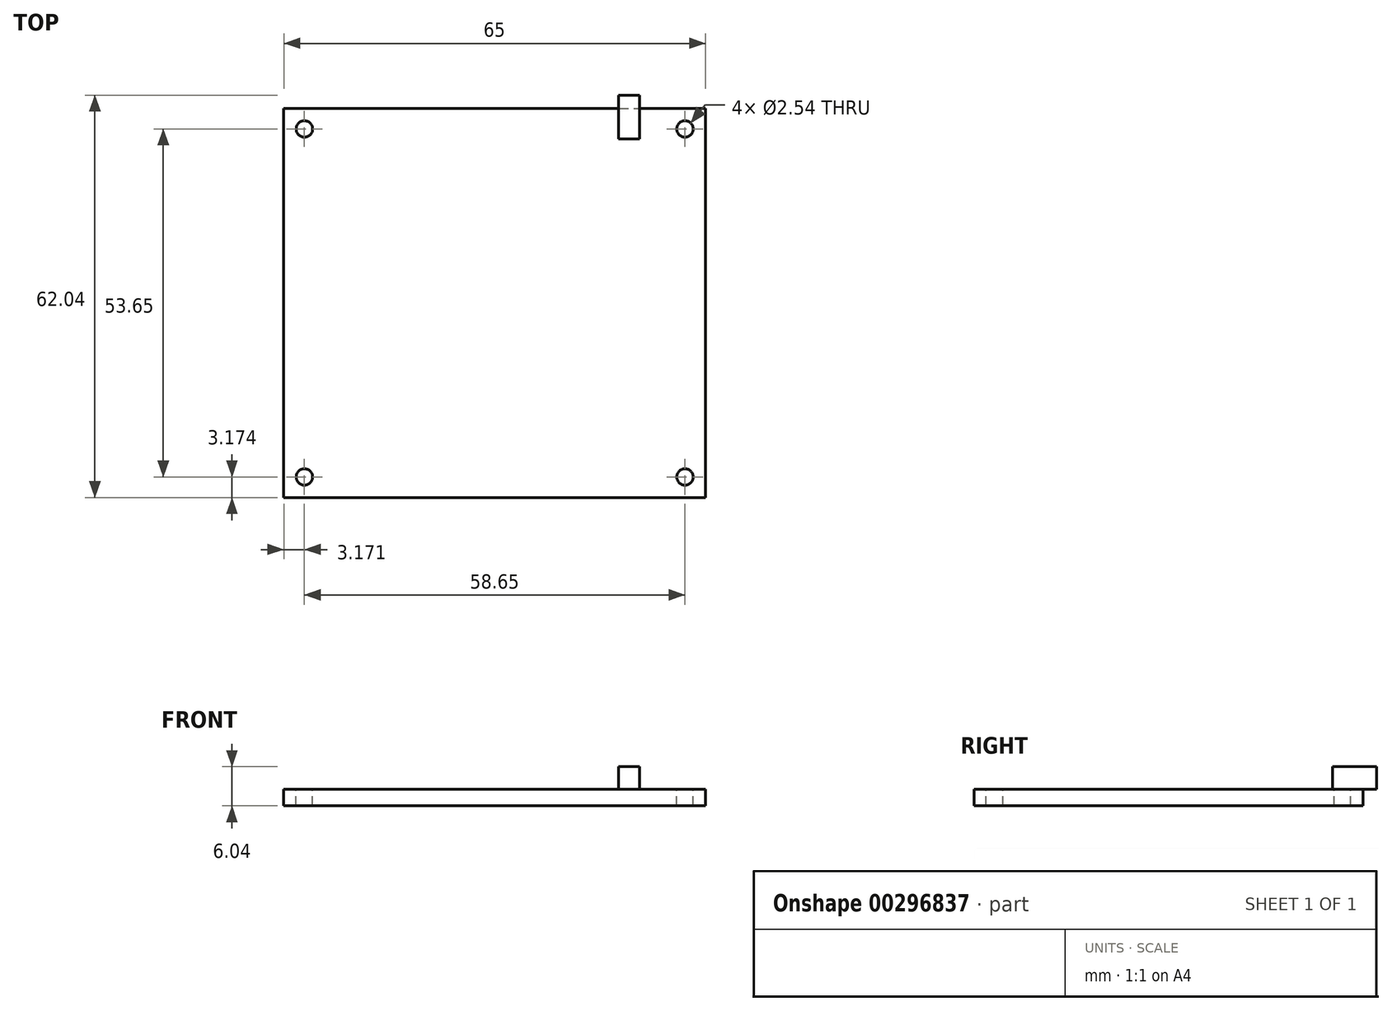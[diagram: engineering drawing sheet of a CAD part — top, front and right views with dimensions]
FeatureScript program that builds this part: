
annotation { "Feature Type Name" : "Feature", "Feature Type Description" : "" }
export const myFeature = defineFeature(function(context is Context, id is Id, definition is map)
    precondition{}
    {
        {
            var Q0;
            Q0=qCreatedBy(makeId("Top.planeOp"),FACE);
            var sketch = newSketch(context, id + "F0", { "sketchPlane" : qUnion([Q0])});
            skLineSegment(sketch, "E0.bottom", {"start": v(21.09, -101.87) * mm, "end": v(86.09, -101.87) * mm});
            skLineSegment(sketch, "E0.top", {"start": v(21.09, -161.87) * mm, "end": v(86.09, -161.87) * mm});
            skLineSegment(sketch, "E0.left", {"start": v(21.09, -101.87) * mm, "end": v(21.09, -161.87) * mm});
            skLineSegment(sketch, "E0.right", {"start": v(86.09, -101.87) * mm, "end": v(86.09, -161.87) * mm});
            skLineSegment(sketch, "E1", {"start": v(21.04, -80.9) * mm, "end": v(108.97, -80.9) * mm});
            skSolve(sketch);
        }
        {
            var Q0;
            Q0=makeQuery(id+"F0.imprint","IMPRINT",FACE,{"disambiguationData":[TD([[makeQuery(id+"F0.imprint","IMPRINT",EDGE,{"derivedFrom":sQuery(id+"F0.wireOp",EDGE,"E0.bottom")}),-1.0]])]});
            extrude(context, id + "F1", {"entities" : qUnion([Q0]), "depth" : 2.54 * mm});
        }
        {
            var Q0;
            Q0=makeQuery(id+"F1.opExtrude","CAP_FACE",FACE,{"disambiguationData":[OSD([sQuery(id+"F0.wireOp",EDGE,"E0.bottom"),sQuery(id+"F0.wireOp",EDGE,"E0.top"),sQuery(id+"F0.wireOp",EDGE,"E0.left"),sQuery(id+"F0.wireOp",EDGE,"E0.right")])],"isStart":false});
            var sketch = newSketch(context, id + "F2", { "sketchPlane" : qUnion([Q0])});
            skLineSegment(sketch, "E2.bottom", {"start": v(24.26, -105.05) * mm, "end": v(82.91, -105.05) * mm, "construction": true});
            skLineSegment(sketch, "E2.top", {"start": v(24.26, -158.7) * mm, "end": v(82.91, -158.7) * mm, "construction": true});
            skLineSegment(sketch, "E2.left", {"start": v(24.26, -105.05) * mm, "end": v(24.26, -158.7) * mm, "construction": true});
            skLineSegment(sketch, "E2.right", {"start": v(82.91, -105.05) * mm, "end": v(82.91, -158.7) * mm, "construction": true});
            skCircle(sketch, "E3", {"center": v(24.26, -105.05) * mm, "radius": 1.27 * mm});
            skCircle(sketch, "E4", {"center": v(82.91, -105.05) * mm, "radius": 1.27 * mm});
            skCircle(sketch, "E5", {"center": v(82.91, -158.7) * mm, "radius": 1.27 * mm});
            skCircle(sketch, "E6", {"center": v(24.26, -158.7) * mm, "radius": 1.27 * mm});
            skSolve(sketch);
        }
        {
            var Q0;
            Q0 = qSketchRegion(id + "F2", true);
            extrude(context, id + "F3", {"entities" : qUnion([Q0]), "operationType" : NewBodyOperationType.REMOVE, "endBound" : BoundingType.THROUGH_ALL, "oppositeDirection" : true, "depth" : 25.4 * mm});
        }
        {
            var Q0;
            Q0=makeQuery(id+"F1.opExtrude","CAP_FACE",FACE,{"disambiguationData":[OSD([sQuery(id+"F0.wireOp",EDGE,"E0.bottom"),sQuery(id+"F0.wireOp",EDGE,"E0.top"),sQuery(id+"F0.wireOp",EDGE,"E0.left"),sQuery(id+"F0.wireOp",EDGE,"E0.right")])],"isStart":false});
            var sketch = newSketch(context, id + "F4", { "sketchPlane" : qUnion([Q0])});
            skLineSegment(sketch, "E7.bottom", {"start": v(75.9, -106.58) * mm, "end": v(72.7, -106.58) * mm});
            skLineSegment(sketch, "E7.top", {"start": v(75.9, -99.83) * mm, "end": v(72.7, -99.83) * mm});
            skLineSegment(sketch, "E7.left", {"start": v(75.9, -106.58) * mm, "end": v(75.9, -99.83) * mm});
            skLineSegment(sketch, "E7.right", {"start": v(72.7, -106.58) * mm, "end": v(72.7, -99.83) * mm});
            skSolve(sketch);
        }
        {
            var Q0;
            Q0 = qSketchRegion(id + "F4", true);
            extrude(context, id + "F5", {"entities" : qUnion([Q0]), "operationType" : NewBodyOperationType.ADD, "depth" : 3.5 * mm});
        }
    });
